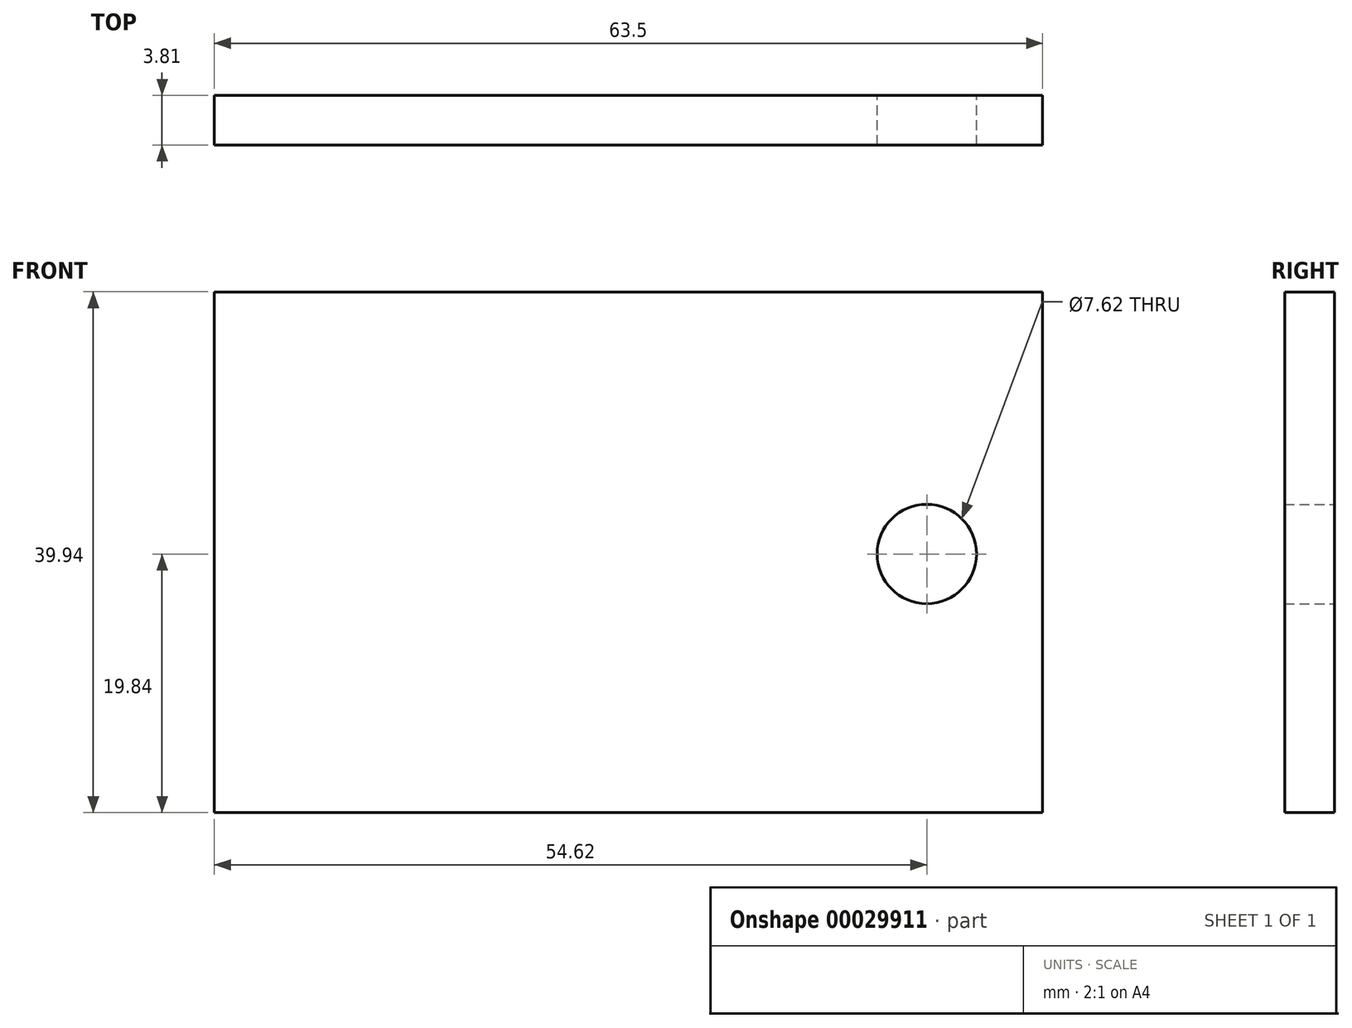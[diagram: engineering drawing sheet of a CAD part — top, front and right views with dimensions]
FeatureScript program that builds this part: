
annotation { "Feature Type Name" : "Feature", "Feature Type Description" : "" }
export const myFeature = defineFeature(function(context is Context, id is Id, definition is map)
    precondition{}
    {
        {
            var Q0;
            Q0=qCreatedBy(makeId("Front.planeOp"),FACE);
            var sketch = newSketch(context, id + "F0", { "sketchPlane" : qUnion([Q0])});
            skLineSegment(sketch, "E0.bottom", {"start": v(-54.62, 23.25) * mm, "end": v(8.88, 23.25) * mm});
            skLineSegment(sketch, "E0.top", {"start": v(-54.62, -16.69) * mm, "end": v(8.88, -16.69) * mm});
            skLineSegment(sketch, "E0.left", {"start": v(-54.62, 23.25) * mm, "end": v(-54.62, -16.69) * mm});
            skLineSegment(sketch, "E0.right", {"start": v(8.88, 23.25) * mm, "end": v(8.88, -16.69) * mm});
            skCircle(sketch, "E1", {"center": v(22.64, 2.35) * mm, "radius": 3.81 * mm});
            skCircle(sketch, "E2", {"center": v(0, 3.15) * mm, "radius": 3.81 * mm});
            skSolve(sketch);
        }
        {
            var Q0;
            Q0=makeQuery(id+"F0.imprint","IMPRINT",FACE,{"disambiguationData":[TD([[makeQuery(id+"F0.imprint","IMPRINT",EDGE,{"derivedFrom":sQuery(id+"F0.wireOp",EDGE,"E0.bottom")}),-1.0]])]});
            extrude(context, id + "F1", {"entities" : qUnion([Q0]), "depth" : 3.8 * mm});
        }
    });
